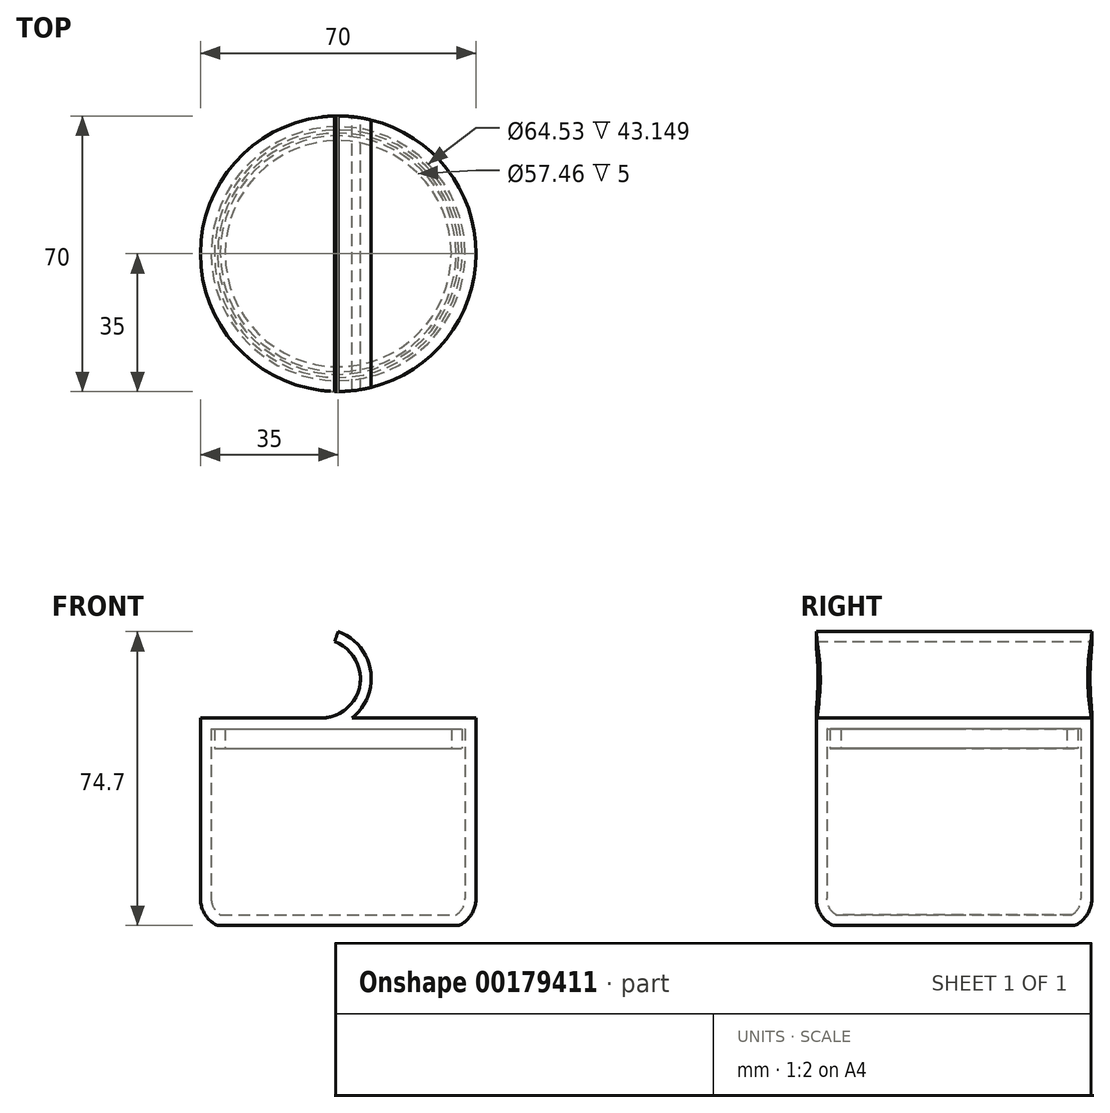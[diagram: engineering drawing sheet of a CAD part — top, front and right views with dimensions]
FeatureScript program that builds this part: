
annotation { "Feature Type Name" : "Feature", "Feature Type Description" : "" }
export const myFeature = defineFeature(function(context is Context, id is Id, definition is map)
    precondition{}
    {
        {
            var Q0;
            Q0=qCreatedBy(makeId("Front.planeOp"),FACE);
            var sketch = newSketch(context, id + "F0", { "sketchPlane" : qUnion([Q0])});
            skLineSegment(sketch, "E0", {"start": v(0, 0) * mm, "end": v(-30.64, 0) * mm});
            skArc(sketch, "E1", {"start": v(-30.64, 0) * mm, "mid": v(-33.82, 2.79) * mm, "end": v(-35, 6.85) * mm});
            skLineSegment(sketch, "E2", {"start": v(-35, 6.85) * mm, "end": v(-35, 50) * mm});
            skLineSegment(sketch, "E3.0", {"start": v(-32.26, 6.85) * mm, "end": v(-32.26, 50) * mm});
            skArc(sketch, "E3.1", {"start": v(-29.96, 2.74) * mm, "mid": v(-31.65, 4.5) * mm, "end": v(-32.26, 6.85) * mm});
            skLineSegment(sketch, "E3.3", {"start": v(0, 2.74) * mm, "end": v(-29.96, 2.74) * mm});
            skLineSegment(sketch, "E4", {"start": v(-35, 50) * mm, "end": v(-32.26, 50) * mm});
            skLineSegment(sketch, "E5", {"start": v(0, 0) * mm, "end": v(0, 50) * mm, "construction": true});
            skLineSegment(sketch, "E6", {"start": v(0, 0) * mm, "end": v(0, 2.74) * mm});
            skLineSegment(sketch, "E7", {"start": v(-30.64, 0) * mm, "end": v(-35, 2.04) * mm, "construction": true});
            skLineSegment(sketch, "E8", {"start": v(-35, 50) * mm, "end": v(-35, 52.74) * mm});
            skLineSegment(sketch, "E9", {"start": v(-35, 52.74) * mm, "end": v(0, 52.74) * mm});
            skLineSegment(sketch, "E10", {"start": v(-31.46, 45) * mm, "end": v(-31.46, 50) * mm});
            skLineSegment(sketch, "E11", {"start": v(-31.46, 50) * mm, "end": v(-32.26, 50) * mm});
            skLineSegment(sketch, "E12", {"start": v(0, 52.74) * mm, "end": v(0, 50) * mm});
            skLineSegment(sketch, "E13", {"start": v(0, 50) * mm, "end": v(-28.73, 50) * mm});
            skLineSegment(sketch, "E14", {"start": v(-28.73, 50) * mm, "end": v(-28.73, 45) * mm});
            skLineSegment(sketch, "E15", {"start": v(-28.73, 45) * mm, "end": v(-31.46, 45) * mm});
            skSolve(sketch);
        }
        {
            var Q0;
            Q0=makeQuery(id+"F0.imprint","IMPRINT",FACE,{"disambiguationData":[TD([[makeQuery(id+"F0.imprint","IMPRINT",EDGE,{"derivedFrom":sQuery(id+"F0.wireOp",EDGE,"E0")}),-1.0]])]});
            var Q1;
            Q1=sQuery(id+"F0.wireOp",EDGE,"E5");
            revolve(context, id + "F1", {"entities" : qUnion([Q0]), "axis" : qUnion([Q1]), "revolveType" : RevolveType.FULL});
        }
        {
            var Q0;
            Q0=makeQuery(id+"F0.imprint","IMPRINT",FACE,{"disambiguationData":[TD([[makeQuery(id+"F0.imprint","IMPRINT",EDGE,{"derivedFrom":sQuery(id+"F0.wireOp",EDGE,"E4")}),1.0]])]});
            var Q1;
            Q1=sQuery(id+"F0.wireOp",EDGE,"E5");
            revolve(context, id + "F2", {"entities" : qUnion([Q0]), "axis" : qUnion([Q1]), "revolveType" : RevolveType.FULL});
        }
        {
            var Q0;
            Q0=qCreatedBy(makeId("Front.planeOp"),FACE);
            var sketch = newSketch(context, id + "F3", { "sketchPlane" : qUnion([Q0])});
            skLineSegment(sketch, "E16.0", {"start": v(35, 52.74) * mm, "end": v(-35, 52.74) * mm, "construction": true});
            skLineSegment(sketch, "E17", {"start": v(-35, 50) * mm, "end": v(-4.36, 50) * mm, "construction": true});
            skArc(sketch, "E18", {"start": v(-4.36, 50) * mm, "mid": v(8.19, 60.52) * mm, "end": v(0, 74.7) * mm});
            skArc(sketch, "E19.0", {"start": v(-4.36, 52.74) * mm, "mid": v(5.5, 61) * mm, "end": v(-0.94, 72.13) * mm});
            skLineSegment(sketch, "E20", {"start": v(-4.36, 52.74) * mm, "end": v(-4.36, 50) * mm});
            skLineSegment(sketch, "E21", {"start": v(-0.94, 72.13) * mm, "end": v(0, 74.7) * mm});
            skLineSegment(sketch, "E22", {"start": v(3.53, 52.74) * mm, "end": v(15.19, 61.93) * mm, "construction": true});
            skSolve(sketch);
        }
        {
            var Q0;
            Q0=makeQuery(id+"F3.imprint","IMPRINT",FACE,{"disambiguationData":[TD([[makeQuery(id+"F3.imprint","IMPRINT",EDGE,{"derivedFrom":sQuery(id+"F3.wireOp",EDGE,"E18")}),1.0]])]});
            var Q1;
            Q1=makeQuery(id+"F2.opRevolve","SWEPT_FACE",FACE,{"disambiguationData":[OSD([sQuery(id+"F0.wireOp",EDGE,"E8")])]});
            var Q2;
            Q2=makeQuery(id+"F2.opRevolve","SWEPT_FACE",FACE,{"disambiguationData":[OSD([sQuery(id+"F0.wireOp",EDGE,"E8")])]});
            extrude(context, id + "F4", {"entities" : qUnion([Q0]), "operationType" : NewBodyOperationType.ADD, "endBound" : BoundingType.UP_TO_SURFACE, "endBoundEntityFace" : qUnion([Q1]), "depth" : 25 * mm, "hasSecondDirection" : true, "secondDirectionBound" : SecondDirectionBoundingType.UP_TO_SURFACE, "secondDirectionOppositeDirection" : true, "secondDirectionBoundEntityFace" : qUnion([Q2]), "secondDirectionDepth" : 25 * mm});
        }
    });
